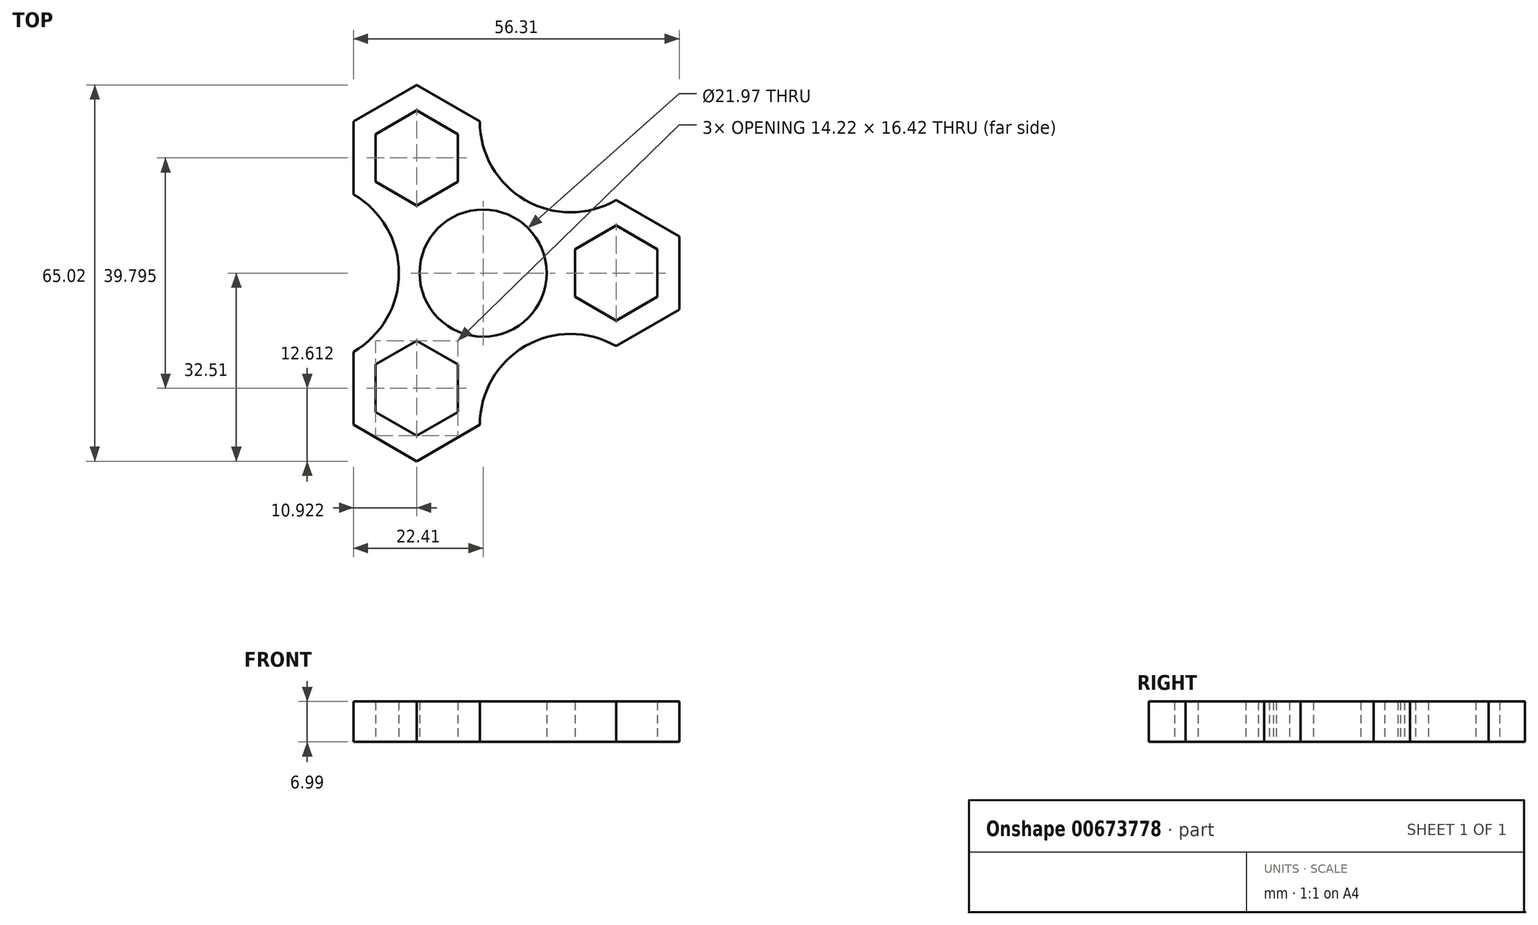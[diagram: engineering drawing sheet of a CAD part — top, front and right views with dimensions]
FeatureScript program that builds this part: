
annotation { "Feature Type Name" : "Feature", "Feature Type Description" : "" }
export const myFeature = defineFeature(function(context is Context, id is Id, definition is map)
    precondition{}
    {
        {
            var Q0;
            Q0=qCreatedBy(makeId("Top.planeOp"),FACE);
            var sketch = newSketch(context, id + "F0", { "sketchPlane" : qUnion([Q0])});
            skCircle(sketch, "E0", {"center": v(0, 0) * mm, "radius": 10.99 * mm});
            skLineSegment(sketch, "E1.0", {"start": v(15.86, -4.1) * mm, "end": v(15.86, 4.1) * mm});
            skLineSegment(sketch, "E1.1", {"start": v(15.86, 4.1) * mm, "end": v(22.98, 8.21) * mm});
            skLineSegment(sketch, "E1.2", {"start": v(22.98, 8.21) * mm, "end": v(30.09, 4.1) * mm});
            skLineSegment(sketch, "E1.3", {"start": v(30.09, 4.1) * mm, "end": v(30.09, -4.1) * mm});
            skLineSegment(sketch, "E1.4", {"start": v(30.09, -4.1) * mm, "end": v(22.98, -8.21) * mm});
            skLineSegment(sketch, "E1.5", {"start": v(22.98, -8.21) * mm, "end": v(15.86, -4.1) * mm});
            skPoint(sketch, "E1.0.midPoint", {"position": v(15.86, 0) * mm});
            skPoint(sketch, "E2.1.0", {"position": v(-7.93, 13.74) * mm});
            skLineSegment(sketch, "E2.1.1", {"start": v(-4.38, 24) * mm, "end": v(-4.38, 15.8) * mm});
            skLineSegment(sketch, "E2.1.2", {"start": v(-11.49, 28.1) * mm, "end": v(-4.38, 24) * mm});
            skLineSegment(sketch, "E2.1.3", {"start": v(-18.6, 24) * mm, "end": v(-11.49, 28.1) * mm});
            skLineSegment(sketch, "E2.1.4", {"start": v(-18.6, 15.8) * mm, "end": v(-18.6, 24) * mm});
            skLineSegment(sketch, "E2.1.5", {"start": v(-11.49, 11.69) * mm, "end": v(-18.6, 15.8) * mm});
            skLineSegment(sketch, "E2.1.6", {"start": v(-4.38, 15.8) * mm, "end": v(-11.49, 11.69) * mm});
            skPoint(sketch, "E2.2.0", {"position": v(-7.93, -13.74) * mm});
            skLineSegment(sketch, "E2.2.1", {"start": v(-18.6, -15.8) * mm, "end": v(-11.49, -11.69) * mm});
            skLineSegment(sketch, "E2.2.2", {"start": v(-18.6, -24) * mm, "end": v(-18.6, -15.8) * mm});
            skLineSegment(sketch, "E2.2.3", {"start": v(-11.49, -28.1) * mm, "end": v(-18.6, -24) * mm});
            skLineSegment(sketch, "E2.2.4", {"start": v(-4.38, -24) * mm, "end": v(-11.49, -28.1) * mm});
            skLineSegment(sketch, "E2.2.5", {"start": v(-4.38, -15.8) * mm, "end": v(-4.38, -24) * mm});
            skLineSegment(sketch, "E2.2.6", {"start": v(-11.49, -11.69) * mm, "end": v(-4.38, -15.8) * mm});
            skLineSegment(sketch, "E3.0", {"start": v(-0.57, 26.2) * mm, "end": v(-0.57, 26.2) * mm});
            skLineSegment(sketch, "E3.2", {"start": v(-22.4, 13.6) * mm, "end": v(-22.4, 26.2) * mm});
            skLineSegment(sketch, "E3.4", {"start": v(-22.4, 26.2) * mm, "end": v(-11.49, 32.5) * mm});
            skLineSegment(sketch, "E3.5", {"start": v(-11.49, 32.5) * mm, "end": v(-0.57, 26.2) * mm});
            skLineSegment(sketch, "E4.2", {"start": v(22.98, 12.61) * mm, "end": v(33.9, 6.3) * mm});
            skLineSegment(sketch, "E4.4", {"start": v(33.9, 6.3) * mm, "end": v(33.9, -6.3) * mm});
            skLineSegment(sketch, "E4.5", {"start": v(33.9, -6.3) * mm, "end": v(22.98, -12.6) * mm});
            skLineSegment(sketch, "E5.0", {"start": v(-0.57, -26.2) * mm, "end": v(-11.49, -32.5) * mm});
            skLineSegment(sketch, "E5.1", {"start": v(-22.4, -26.2) * mm, "end": v(-22.4, -13.6) * mm});
            skLineSegment(sketch, "E5.3", {"start": v(-11.49, -32.5) * mm, "end": v(-22.4, -26.2) * mm});
            skArc(sketch, "E6", {"start": v(-22.4, -13.6) * mm, "mid": v(-14.56, 0) * mm, "end": v(-22.4, 13.6) * mm});
            skArc(sketch, "E7", {"start": v(22.98, -12.6) * mm, "mid": v(7.28, -12.6) * mm, "end": v(-0.57, -26.2) * mm});
            skArc(sketch, "E8", {"start": v(-0.57, 26.2) * mm, "mid": v(7.28, 12.61) * mm, "end": v(22.98, 12.61) * mm});
            skSolve(sketch);
        }
        {
            var Q0;
            Q0=makeQuery(id+"F0.imprint","IMPRINT",FACE,{"disambiguationData":[TD([[makeQuery(id+"F0.imprint","IMPRINT",EDGE,{"derivedFrom":sQuery(id+"F0.wireOp",EDGE,"E0")}),-1.0]])]});
            extrude(context, id + "F1", {"entities" : qUnion([Q0]), "depth" : 7 * mm, "offsetDistance" : 25.4 * mm});
        }
    });
